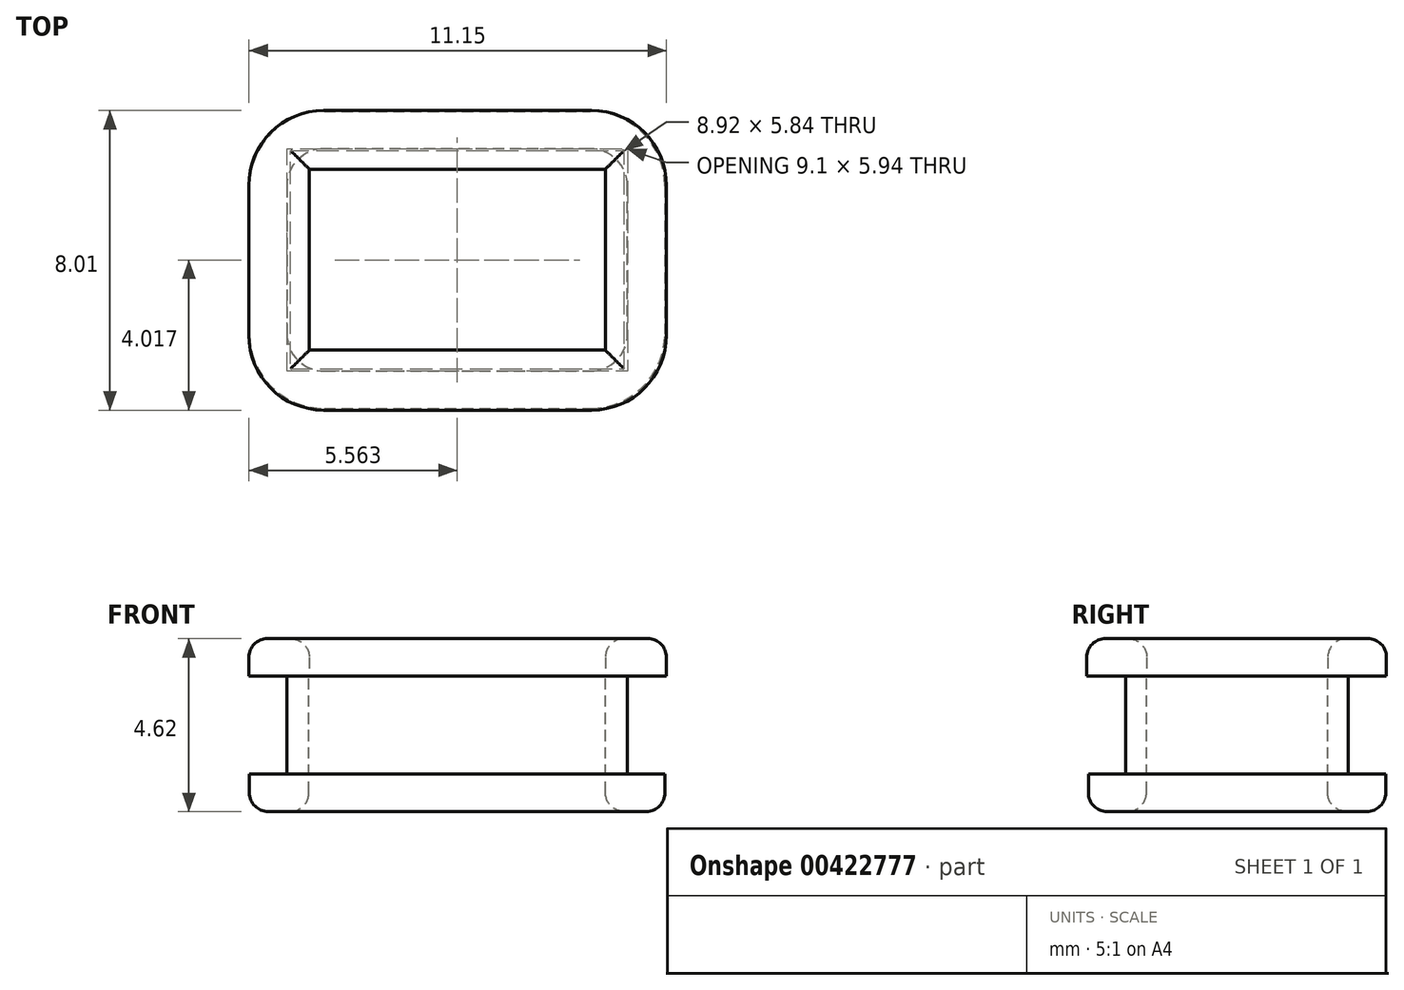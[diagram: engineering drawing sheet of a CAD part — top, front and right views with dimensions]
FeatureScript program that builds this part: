
annotation { "Feature Type Name" : "Feature", "Feature Type Description" : "" }
export const myFeature = defineFeature(function(context is Context, id is Id, definition is map)
    precondition{}
    {
        {
            var Q0;
            Q0=qCreatedBy(makeId("Top.planeOp"),FACE);
            var sketch = newSketch(context, id + "F0", { "sketchPlane" : qUnion([Q0])});
            skLineSegment(sketch, "E0.bottom", {"start": v(2.58, 1.83) * mm, "end": v(13.68, 1.83) * mm});
            skLineSegment(sketch, "E0.top", {"start": v(2.58, -6.11) * mm, "end": v(13.68, -6.11) * mm});
            skLineSegment(sketch, "E0.left", {"start": v(2.58, 1.83) * mm, "end": v(2.58, -6.11) * mm});
            skLineSegment(sketch, "E0.right", {"start": v(13.68, 1.83) * mm, "end": v(13.68, -6.11) * mm});
            skSolve(sketch);
        }
        {
            var Q0;
            Q0 = qSketchRegion(id + "F0", true);
            extrude(context, id + "F1", {"entities" : qUnion([Q0]), "depth" : 1 * mm});
        }
        {
            var Q0;
            Q0=makeQuery(id+"F1.opExtrude","CAP_FACE",FACE,{"disambiguationData":[OSD([sQuery(id+"F0.wireOp",EDGE,"E0.bottom"),sQuery(id+"F0.wireOp",EDGE,"E0.top"),sQuery(id+"F0.wireOp",EDGE,"E0.left"),sQuery(id+"F0.wireOp",EDGE,"E0.right")])],"isStart":false});
            var sketch = newSketch(context, id + "F2", { "sketchPlane" : qUnion([Q0])});
            skLineSegment(sketch, "E1", {"start": v(3.58, -5.11) * mm, "end": v(12.68, -5.11) * mm});
            skLineSegment(sketch, "E2", {"start": v(12.68, -5.11) * mm, "end": v(12.68, 0.83) * mm});
            skLineSegment(sketch, "E3", {"start": v(12.68, 0.83) * mm, "end": v(3.58, 0.83) * mm});
            skLineSegment(sketch, "E4", {"start": v(3.58, 0.83) * mm, "end": v(3.58, -5.11) * mm});
            skLineSegment(sketch, "E5", {"start": v(2.58, -6.11) * mm, "end": v(13.68, -6.11) * mm});
            skLineSegment(sketch, "E6", {"start": v(13.68, -6.11) * mm, "end": v(13.68, 1.83) * mm});
            skLineSegment(sketch, "E7", {"start": v(13.68, 1.83) * mm, "end": v(2.58, 1.83) * mm});
            skLineSegment(sketch, "E8", {"start": v(2.58, 1.83) * mm, "end": v(2.58, -6.11) * mm});
            skSolve(sketch);
        }
        {
            var Q0;
            Q0=makeQuery(id+"F2.imprint","IMPRINT",FACE,{"disambiguationData":[TD([[makeQuery(id+"F2.imprint","IMPRINT",EDGE,{"derivedFrom":sQuery(id+"F2.wireOp",EDGE,"E1")}),1.0]])]});
            extrude(context, id + "F3", {"entities" : qUnion([Q0]), "operationType" : NewBodyOperationType.ADD, "depth" : 2.62 * mm});
        }
        {
            var Q0;
            Q0=makeQuery(id+"F3.opExtrude","CAP_FACE",FACE,{"disambiguationData":[OSD([sQuery(id+"F2.wireOp",EDGE,"E1"),sQuery(id+"F2.wireOp",EDGE,"E2"),sQuery(id+"F2.wireOp",EDGE,"E3"),sQuery(id+"F2.wireOp",EDGE,"E4")])],"isStart":false});
            var sketch = newSketch(context, id + "F4", { "sketchPlane" : qUnion([Q0])});
            skLineSegment(sketch, "E9.bottom", {"start": v(2.59, 1.83) * mm, "end": v(13.67, 1.83) * mm});
            skLineSegment(sketch, "E9.top", {"start": v(2.59, -6.12) * mm, "end": v(13.67, -6.12) * mm});
            skLineSegment(sketch, "E9.left", {"start": v(2.59, 1.83) * mm, "end": v(2.59, -6.12) * mm});
            skLineSegment(sketch, "E9.right", {"start": v(13.67, 1.83) * mm, "end": v(13.67, -6.12) * mm});
            skSolve(sketch);
        }
        {
            var Q0;
            Q0=makeQuery(id+"F4.imprint","IMPRINT",FACE,{"disambiguationData":[TD([[makeQuery(id+"F4.imprint","IMPRINT",EDGE,{"derivedFrom":makeQuery(id+"F3.opExtrude","CAP_EDGE",EDGE,{"disambiguationData":[OSD([sQuery(id+"F2.wireOp",EDGE,"E1")])],"isStart":false})}),1.0]])]});
            var sketch = newSketch(context, id + "F5", { "sketchPlane" : qUnion([Q0])});
            skLineSegment(sketch, "E10.bottom", {"start": v(4.17, 0.28) * mm, "end": v(12.1, 0.28) * mm});
            skLineSegment(sketch, "E10.top", {"start": v(4.17, -4.56) * mm, "end": v(12.1, -4.56) * mm});
            skLineSegment(sketch, "E10.left", {"start": v(4.17, 0.28) * mm, "end": v(4.17, -4.56) * mm});
            skLineSegment(sketch, "E10.right", {"start": v(12.1, 0.28) * mm, "end": v(12.1, -4.56) * mm});
            skSolve(sketch);
        }
        {
            var Q0;
            Q0 = qSketchRegion(id + "F5", true);
            extrude(context, id + "F6", {"entities" : qUnion([Q0]), "operationType" : NewBodyOperationType.REMOVE, "oppositeDirection" : true, "depth" : 25 * mm});
        }
        {
            var Q0;
            Q0=makeQuery(id+"F4.imprint","IMPRINT",FACE,{"disambiguationData":[TD([[makeQuery(id+"F4.imprint","IMPRINT",EDGE,{"derivedFrom":makeQuery(id+"F3.opExtrude","CAP_EDGE",EDGE,{"disambiguationData":[OSD([sQuery(id+"F2.wireOp",EDGE,"E1")])],"isStart":false})}),1.0]])]});
            var sketch = newSketch(context, id + "F7", { "sketchPlane" : qUnion([Q0])});
            skLineSegment(sketch, "E11.bottom", {"start": v(2.57, 1.85) * mm, "end": v(13.72, 1.85) * mm});
            skLineSegment(sketch, "E11.top", {"start": v(2.57, -6.16) * mm, "end": v(13.72, -6.16) * mm});
            skLineSegment(sketch, "E11.left", {"start": v(2.57, 1.85) * mm, "end": v(2.57, -6.16) * mm});
            skLineSegment(sketch, "E11.right", {"start": v(13.72, 1.85) * mm, "end": v(13.72, -6.16) * mm});
            skSolve(sketch);
        }
        {
            var Q0;
            Q0 = qSketchRegion(id + "F7", true);
            extrude(context, id + "F8", {"entities" : qUnion([Q0]), "operationType" : NewBodyOperationType.ADD, "depth" : 1 * mm});
        }
        {
            var Q0;
            Q0=makeQuery(id+"F4.imprint","IMPRINT",FACE,{"disambiguationData":[TD([[makeQuery(id+"F4.imprint","IMPRINT",EDGE,{"derivedFrom":makeQuery(id+"F3.opExtrude","CAP_EDGE",EDGE,{"disambiguationData":[OSD([sQuery(id+"F2.wireOp",EDGE,"E1")])],"isStart":false})}),1.0]])]});
            var sketch = newSketch(context, id + "F9", { "sketchPlane" : qUnion([Q0])});
            skLineSegment(sketch, "E12.bottom", {"start": v(12.1, 0.28) * mm, "end": v(4.18, 0.28) * mm});
            skLineSegment(sketch, "E12.top", {"start": v(12.1, -4.55) * mm, "end": v(4.18, -4.55) * mm});
            skLineSegment(sketch, "E12.left", {"start": v(12.1, 0.28) * mm, "end": v(12.1, -4.55) * mm});
            skLineSegment(sketch, "E12.right", {"start": v(4.18, 0.28) * mm, "end": v(4.18, -4.55) * mm});
            skSolve(sketch);
        }
        {
            var Q0;
            Q0 = qSketchRegion(id + "F9", true);
            extrude(context, id + "F10", {"entities" : qUnion([Q0]), "operationType" : NewBodyOperationType.REMOVE, "depth" : 8.5 * mm});
        }
        {
            var Q0;
            Q0=makeQuery(id+"F8.opExtrude","SWEPT_EDGE",EDGE,{"disambiguationData":[OSD([sQuery(id+"F7.wireOp",EDGE,"E11.bottom"),sQuery(id+"F7.wireOp",EDGE,"E11.right")])]});
            var Q1;
            Q1=makeQuery(id+"F8.opExtrude","SWEPT_EDGE",EDGE,{"disambiguationData":[OSD([sQuery(id+"F7.wireOp",EDGE,"E11.bottom"),sQuery(id+"F7.wireOp",EDGE,"E11.left")])]});
            var Q2;
            Q2=makeQuery(id+"F8.opExtrude","SWEPT_EDGE",EDGE,{"disambiguationData":[OSD([sQuery(id+"F7.wireOp",EDGE,"E11.top"),sQuery(id+"F7.wireOp",EDGE,"E11.left")])]});
            var Q3;
            Q3=makeQuery(id+"F8.opExtrude","SWEPT_EDGE",EDGE,{"disambiguationData":[OSD([sQuery(id+"F7.wireOp",EDGE,"E11.top"),sQuery(id+"F7.wireOp",EDGE,"E11.right")])]});
            var Q4;
            Q4=makeQuery(id+"F1.opExtrude","SWEPT_EDGE",EDGE,{"disambiguationData":[OSD([sQuery(id+"F0.wireOp",EDGE,"E0.bottom"),sQuery(id+"F0.wireOp",EDGE,"E0.left")])]});
            var Q5;
            Q5=makeQuery(id+"F1.opExtrude","SWEPT_EDGE",EDGE,{"disambiguationData":[OSD([sQuery(id+"F0.wireOp",EDGE,"E0.top"),sQuery(id+"F0.wireOp",EDGE,"E0.left")])]});
            var Q6;
            Q6=makeQuery(id+"F1.opExtrude","SWEPT_EDGE",EDGE,{"disambiguationData":[OSD([sQuery(id+"F0.wireOp",EDGE,"E0.top"),sQuery(id+"F0.wireOp",EDGE,"E0.right")])]});
            var Q7;
            Q7=makeQuery(id+"F1.opExtrude","SWEPT_EDGE",EDGE,{"disambiguationData":[OSD([sQuery(id+"F0.wireOp",EDGE,"E0.bottom"),sQuery(id+"F0.wireOp",EDGE,"E0.right")])]});
            fillet(context, id + "F11", {"entities" : qUnion([Q0, Q1, Q2, Q3, Q4, Q5, Q6, Q7]), "radius" : 2 * mm, "tangentPropagation" : true, "allowEdgeOverflow" : false});
        }
        {
            var Q0;
            Q0=makeQuery(id+"F3.opExtrude","SWEPT_EDGE",EDGE,{"disambiguationData":[OSD([sQuery(id+"F2.wireOp",EDGE,"E1"),sQuery(id+"F2.wireOp",EDGE,"E2")])]});
            var Q1;
            Q1=makeQuery(id+"F3.opExtrude","SWEPT_EDGE",EDGE,{"disambiguationData":[OSD([sQuery(id+"F2.wireOp",EDGE,"E1"),sQuery(id+"F2.wireOp",EDGE,"E4")])]});
            var Q2;
            Q2=makeQuery(id+"F3.opExtrude","SWEPT_EDGE",EDGE,{"disambiguationData":[OSD([sQuery(id+"F2.wireOp",EDGE,"E3"),sQuery(id+"F2.wireOp",EDGE,"E4")])]});
            var Q3;
            Q3=makeQuery(id+"F3.opExtrude","SWEPT_EDGE",EDGE,{"disambiguationData":[OSD([sQuery(id+"F2.wireOp",EDGE,"E2"),sQuery(id+"F2.wireOp",EDGE,"E3")])]});
            fillet(context, id + "F12", {"entities" : qUnion([Q0, Q1, Q2, Q3]), "radius" : 1 * mm, "tangentPropagation" : true, "allowEdgeOverflow" : false});
        }
        {
            var Q0;
            Q0=makeQuery(id+"F6.boolean.opBoolean","INTERSECT",EDGE,{"derivedFrom":[makeQuery(id+"F1.opExtrude","CAP_FACE",FACE,{"disambiguationData":[OSD([sQuery(id+"F0.wireOp",EDGE,"E0.bottom"),sQuery(id+"F0.wireOp",EDGE,"E0.top"),sQuery(id+"F0.wireOp",EDGE,"E0.left"),sQuery(id+"F0.wireOp",EDGE,"E0.right")])],"isStart":true}),makeQuery(id+"F6.opExtrude","SWEPT_FACE",FACE,{"disambiguationData":[OSD([sQuery(id+"F5.wireOp",EDGE,"E10.top")])]})]});
            var Q1;
            Q1=makeQuery(id+"F6.boolean.opBoolean","INTERSECT",EDGE,{"derivedFrom":[makeQuery(id+"F1.opExtrude","CAP_FACE",FACE,{"disambiguationData":[OSD([sQuery(id+"F0.wireOp",EDGE,"E0.bottom"),sQuery(id+"F0.wireOp",EDGE,"E0.top"),sQuery(id+"F0.wireOp",EDGE,"E0.left"),sQuery(id+"F0.wireOp",EDGE,"E0.right")])],"isStart":true}),makeQuery(id+"F6.opExtrude","SWEPT_FACE",FACE,{"disambiguationData":[OSD([sQuery(id+"F5.wireOp",EDGE,"E10.right")])]})]});
            var Q2;
            Q2=makeQuery(id+"F6.boolean.opBoolean","INTERSECT",EDGE,{"derivedFrom":[makeQuery(id+"F1.opExtrude","CAP_FACE",FACE,{"disambiguationData":[OSD([sQuery(id+"F0.wireOp",EDGE,"E0.bottom"),sQuery(id+"F0.wireOp",EDGE,"E0.top"),sQuery(id+"F0.wireOp",EDGE,"E0.left"),sQuery(id+"F0.wireOp",EDGE,"E0.right")])],"isStart":true}),makeQuery(id+"F6.opExtrude","SWEPT_FACE",FACE,{"disambiguationData":[OSD([sQuery(id+"F5.wireOp",EDGE,"E10.bottom")])]})]});
            var Q3;
            Q3=makeQuery(id+"F6.boolean.opBoolean","INTERSECT",EDGE,{"derivedFrom":[makeQuery(id+"F1.opExtrude","CAP_FACE",FACE,{"disambiguationData":[OSD([sQuery(id+"F0.wireOp",EDGE,"E0.bottom"),sQuery(id+"F0.wireOp",EDGE,"E0.top"),sQuery(id+"F0.wireOp",EDGE,"E0.left"),sQuery(id+"F0.wireOp",EDGE,"E0.right")])],"isStart":true}),makeQuery(id+"F6.opExtrude","SWEPT_FACE",FACE,{"disambiguationData":[OSD([sQuery(id+"F5.wireOp",EDGE,"E10.left")])]})]});
            var Q4;
            Q4=makeQuery(id+"F10.boolean.opBoolean","INTERSECT",EDGE,{"derivedFrom":[makeQuery(id+"F8.opExtrude","CAP_FACE",FACE,{"disambiguationData":[OSD([sQuery(id+"F7.wireOp",EDGE,"E11.bottom"),sQuery(id+"F7.wireOp",EDGE,"E11.top"),sQuery(id+"F7.wireOp",EDGE,"E11.left"),sQuery(id+"F7.wireOp",EDGE,"E11.right")])],"isStart":false}),makeQuery(id+"F10.opExtrude","SWEPT_FACE",FACE,{"disambiguationData":[OSD([sQuery(id+"F9.wireOp",EDGE,"E12.left")])]})]});
            var Q5;
            Q5=makeQuery(id+"F10.boolean.opBoolean","INTERSECT",EDGE,{"derivedFrom":[makeQuery(id+"F8.opExtrude","CAP_FACE",FACE,{"disambiguationData":[OSD([sQuery(id+"F7.wireOp",EDGE,"E11.bottom"),sQuery(id+"F7.wireOp",EDGE,"E11.top"),sQuery(id+"F7.wireOp",EDGE,"E11.left"),sQuery(id+"F7.wireOp",EDGE,"E11.right")])],"isStart":false}),makeQuery(id+"F10.opExtrude","SWEPT_FACE",FACE,{"disambiguationData":[OSD([sQuery(id+"F9.wireOp",EDGE,"E12.top")])]})]});
            var Q6;
            Q6=makeQuery(id+"F10.boolean.opBoolean","INTERSECT",EDGE,{"derivedFrom":[makeQuery(id+"F8.opExtrude","CAP_FACE",FACE,{"disambiguationData":[OSD([sQuery(id+"F7.wireOp",EDGE,"E11.bottom"),sQuery(id+"F7.wireOp",EDGE,"E11.top"),sQuery(id+"F7.wireOp",EDGE,"E11.left"),sQuery(id+"F7.wireOp",EDGE,"E11.right")])],"isStart":false}),makeQuery(id+"F10.opExtrude","SWEPT_FACE",FACE,{"disambiguationData":[OSD([sQuery(id+"F9.wireOp",EDGE,"E12.bottom")])]})]});
            var Q7;
            Q7=makeQuery(id+"F10.boolean.opBoolean","INTERSECT",EDGE,{"derivedFrom":[makeQuery(id+"F8.opExtrude","CAP_FACE",FACE,{"disambiguationData":[OSD([sQuery(id+"F7.wireOp",EDGE,"E11.bottom"),sQuery(id+"F7.wireOp",EDGE,"E11.top"),sQuery(id+"F7.wireOp",EDGE,"E11.left"),sQuery(id+"F7.wireOp",EDGE,"E11.right")])],"isStart":false}),makeQuery(id+"F10.opExtrude","SWEPT_FACE",FACE,{"disambiguationData":[OSD([sQuery(id+"F9.wireOp",EDGE,"E12.right")])]})]});
            fillet(context, id + "F13", {"entities" : qUnion([Q0, Q1, Q2, Q3, Q4, Q5, Q6, Q7]), "radius" : 0.5 * mm, "tangentPropagation" : true, "allowEdgeOverflow" : false});
        }
        {
            var Q0;
            Q0=makeQuery(id+"F8.opExtrude","CAP_EDGE",EDGE,{"disambiguationData":[OSD([sQuery(id+"F7.wireOp",EDGE,"E11.bottom")])],"isStart":false});
            var Q1;
            {var subQ0=sQuery(id+"F7.wireOp",EDGE,"E11.right");var subQ1=sQuery(id+"F7.wireOp",EDGE,"E11.bottom");Q1=makeQuery(id+"F11.opFillet","BLEND_EDGE",EDGE,{"blendedFrom":[makeQuery(id+"F8.opExtrude","SWEPT_EDGE",EDGE,{"disambiguationData":[OSD([subQ1,subQ0])]}),makeQuery(id+"F8.opExtrude","CAP_FACE",FACE,{"disambiguationData":[OSD([subQ1,sQuery(id+"F7.wireOp",EDGE,"E11.top"),sQuery(id+"F7.wireOp",EDGE,"E11.left"),subQ0])],"isStart":false})],"blendedInto":[makeQuery(id+"F8.opExtrude","CAP_FACE",FACE,{"disambiguationData":[OSD([subQ1,sQuery(id+"F7.wireOp",EDGE,"E11.top"),sQuery(id+"F7.wireOp",EDGE,"E11.left"),subQ0])],"isStart":false})]});}
            var Q2;
            Q2=makeQuery(id+"F8.opExtrude","CAP_EDGE",EDGE,{"disambiguationData":[OSD([sQuery(id+"F7.wireOp",EDGE,"E11.right")])],"isStart":false});
            var Q3;
            {var subQ0=sQuery(id+"F7.wireOp",EDGE,"E11.right");var subQ1=sQuery(id+"F7.wireOp",EDGE,"E11.top");Q3=makeQuery(id+"F11.opFillet","BLEND_EDGE",EDGE,{"blendedFrom":[makeQuery(id+"F8.opExtrude","SWEPT_EDGE",EDGE,{"disambiguationData":[OSD([subQ1,subQ0])]}),makeQuery(id+"F8.opExtrude","CAP_FACE",FACE,{"disambiguationData":[OSD([sQuery(id+"F7.wireOp",EDGE,"E11.bottom"),subQ1,sQuery(id+"F7.wireOp",EDGE,"E11.left"),subQ0])],"isStart":false})],"blendedInto":[makeQuery(id+"F8.opExtrude","CAP_FACE",FACE,{"disambiguationData":[OSD([sQuery(id+"F7.wireOp",EDGE,"E11.bottom"),subQ1,sQuery(id+"F7.wireOp",EDGE,"E11.left"),subQ0])],"isStart":false})]});}
            var Q4;
            Q4=makeQuery(id+"F8.opExtrude","CAP_EDGE",EDGE,{"disambiguationData":[OSD([sQuery(id+"F7.wireOp",EDGE,"E11.top")])],"isStart":false});
            var Q5;
            Q5=makeQuery(id+"F8.opExtrude","CAP_EDGE",EDGE,{"disambiguationData":[OSD([sQuery(id+"F7.wireOp",EDGE,"E11.left")])],"isStart":false});
            var Q6;
            {var subQ0=sQuery(id+"F7.wireOp",EDGE,"E11.left");var subQ1=sQuery(id+"F7.wireOp",EDGE,"E11.top");Q6=makeQuery(id+"F11.opFillet","BLEND_EDGE",EDGE,{"blendedFrom":[makeQuery(id+"F8.opExtrude","SWEPT_EDGE",EDGE,{"disambiguationData":[OSD([subQ1,subQ0])]}),makeQuery(id+"F8.opExtrude","CAP_FACE",FACE,{"disambiguationData":[OSD([sQuery(id+"F7.wireOp",EDGE,"E11.bottom"),subQ1,subQ0,sQuery(id+"F7.wireOp",EDGE,"E11.right")])],"isStart":false})],"blendedInto":[makeQuery(id+"F8.opExtrude","CAP_FACE",FACE,{"disambiguationData":[OSD([sQuery(id+"F7.wireOp",EDGE,"E11.bottom"),subQ1,subQ0,sQuery(id+"F7.wireOp",EDGE,"E11.right")])],"isStart":false})]});}
            var Q7;
            {var subQ0=sQuery(id+"F7.wireOp",EDGE,"E11.left");var subQ1=sQuery(id+"F7.wireOp",EDGE,"E11.bottom");Q7=makeQuery(id+"F11.opFillet","BLEND_EDGE",EDGE,{"blendedFrom":[makeQuery(id+"F8.opExtrude","SWEPT_EDGE",EDGE,{"disambiguationData":[OSD([subQ1,subQ0])]}),makeQuery(id+"F8.opExtrude","CAP_FACE",FACE,{"disambiguationData":[OSD([subQ1,sQuery(id+"F7.wireOp",EDGE,"E11.top"),subQ0,sQuery(id+"F7.wireOp",EDGE,"E11.right")])],"isStart":false})],"blendedInto":[makeQuery(id+"F8.opExtrude","CAP_FACE",FACE,{"disambiguationData":[OSD([subQ1,sQuery(id+"F7.wireOp",EDGE,"E11.top"),subQ0,sQuery(id+"F7.wireOp",EDGE,"E11.right")])],"isStart":false})]});}
            var Q8;
            {var subQ0=sQuery(id+"F0.wireOp",EDGE,"E0.left");var subQ1=sQuery(id+"F0.wireOp",EDGE,"E0.bottom");Q8=makeQuery(id+"F11.opFillet","BLEND_EDGE",EDGE,{"blendedFrom":[makeQuery(id+"F1.opExtrude","SWEPT_EDGE",EDGE,{"disambiguationData":[OSD([subQ1,subQ0])]}),makeQuery(id+"F1.opExtrude","CAP_FACE",FACE,{"disambiguationData":[OSD([subQ1,sQuery(id+"F0.wireOp",EDGE,"E0.top"),subQ0,sQuery(id+"F0.wireOp",EDGE,"E0.right")])],"isStart":true})],"blendedInto":[makeQuery(id+"F1.opExtrude","CAP_FACE",FACE,{"disambiguationData":[OSD([subQ1,sQuery(id+"F0.wireOp",EDGE,"E0.top"),subQ0,sQuery(id+"F0.wireOp",EDGE,"E0.right")])],"isStart":true})]});}
            var Q9;
            Q9=makeQuery(id+"F1.opExtrude","CAP_EDGE",EDGE,{"disambiguationData":[OSD([sQuery(id+"F0.wireOp",EDGE,"E0.left")])],"isStart":true});
            var Q10;
            {var subQ0=sQuery(id+"F0.wireOp",EDGE,"E0.left");var subQ1=sQuery(id+"F0.wireOp",EDGE,"E0.top");Q10=makeQuery(id+"F11.opFillet","BLEND_EDGE",EDGE,{"blendedFrom":[makeQuery(id+"F1.opExtrude","SWEPT_EDGE",EDGE,{"disambiguationData":[OSD([subQ1,subQ0])]}),makeQuery(id+"F1.opExtrude","CAP_FACE",FACE,{"disambiguationData":[OSD([sQuery(id+"F0.wireOp",EDGE,"E0.bottom"),subQ1,subQ0,sQuery(id+"F0.wireOp",EDGE,"E0.right")])],"isStart":true})],"blendedInto":[makeQuery(id+"F1.opExtrude","CAP_FACE",FACE,{"disambiguationData":[OSD([sQuery(id+"F0.wireOp",EDGE,"E0.bottom"),subQ1,subQ0,sQuery(id+"F0.wireOp",EDGE,"E0.right")])],"isStart":true})]});}
            var Q11;
            Q11=makeQuery(id+"F1.opExtrude","CAP_EDGE",EDGE,{"disambiguationData":[OSD([sQuery(id+"F0.wireOp",EDGE,"E0.top")])],"isStart":true});
            var Q12;
            {var subQ0=sQuery(id+"F0.wireOp",EDGE,"E0.right");var subQ1=sQuery(id+"F0.wireOp",EDGE,"E0.top");Q12=makeQuery(id+"F11.opFillet","BLEND_EDGE",EDGE,{"blendedFrom":[makeQuery(id+"F1.opExtrude","SWEPT_EDGE",EDGE,{"disambiguationData":[OSD([subQ1,subQ0])]}),makeQuery(id+"F1.opExtrude","CAP_FACE",FACE,{"disambiguationData":[OSD([sQuery(id+"F0.wireOp",EDGE,"E0.bottom"),subQ1,sQuery(id+"F0.wireOp",EDGE,"E0.left"),subQ0])],"isStart":true})],"blendedInto":[makeQuery(id+"F1.opExtrude","CAP_FACE",FACE,{"disambiguationData":[OSD([sQuery(id+"F0.wireOp",EDGE,"E0.bottom"),subQ1,sQuery(id+"F0.wireOp",EDGE,"E0.left"),subQ0])],"isStart":true})]});}
            var Q13;
            {var subQ0=sQuery(id+"F0.wireOp",EDGE,"E0.right");var subQ1=sQuery(id+"F0.wireOp",EDGE,"E0.bottom");Q13=makeQuery(id+"F11.opFillet","BLEND_EDGE",EDGE,{"blendedFrom":[makeQuery(id+"F1.opExtrude","SWEPT_EDGE",EDGE,{"disambiguationData":[OSD([subQ1,subQ0])]}),makeQuery(id+"F1.opExtrude","CAP_FACE",FACE,{"disambiguationData":[OSD([subQ1,sQuery(id+"F0.wireOp",EDGE,"E0.top"),sQuery(id+"F0.wireOp",EDGE,"E0.left"),subQ0])],"isStart":true})],"blendedInto":[makeQuery(id+"F1.opExtrude","CAP_FACE",FACE,{"disambiguationData":[OSD([subQ1,sQuery(id+"F0.wireOp",EDGE,"E0.top"),sQuery(id+"F0.wireOp",EDGE,"E0.left"),subQ0])],"isStart":true})]});}
            var Q14;
            Q14=makeQuery(id+"F1.opExtrude","CAP_EDGE",EDGE,{"disambiguationData":[OSD([sQuery(id+"F0.wireOp",EDGE,"E0.right")])],"isStart":true});
            var Q15;
            Q15=makeQuery(id+"F1.opExtrude","CAP_EDGE",EDGE,{"disambiguationData":[OSD([sQuery(id+"F0.wireOp",EDGE,"E0.bottom")])],"isStart":true});
            fillet(context, id + "F14", {"entities" : qUnion([Q0, Q1, Q2, Q3, Q4, Q5, Q6, Q7, Q8, Q9, Q10, Q11, Q12, Q13, Q14, Q15]), "radius" : 0.5 * mm, "tangentPropagation" : true, "allowEdgeOverflow" : false});
        }
    });
